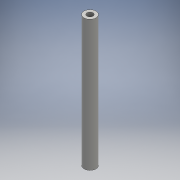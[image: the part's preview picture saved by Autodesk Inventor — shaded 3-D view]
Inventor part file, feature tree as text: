
AUTODESK INVENTOR PART (.ipt)
format: ipt  version: 2016 (Build 200138000, 138)  size: 89,088 bytes
history: native  units: mm
features: other x1, extrude x1, sketch x1
ambient origin geometry x8: Origin, YZ Plane, XZ Plane, XY Plane, X Axis, Y Axis, Z Axis, Center Point
bodies: Body1 (feature_tree)
feature tree (3):
  other  "ソリッド1"
  extrude  "押し出し1"  Depth=6.0mm
  sketch  "スケッチ1"
